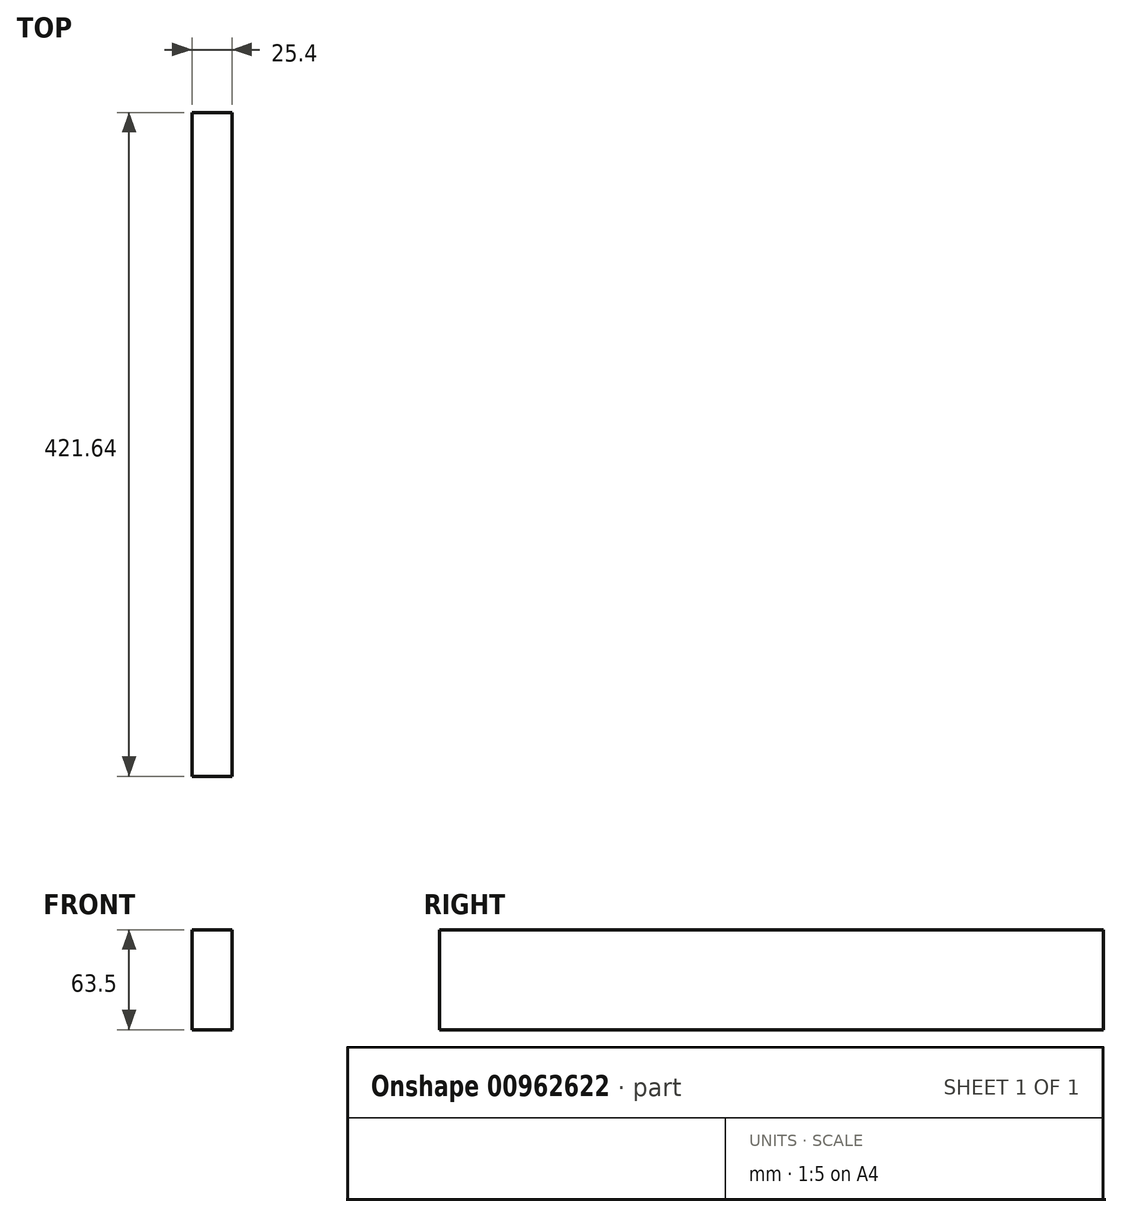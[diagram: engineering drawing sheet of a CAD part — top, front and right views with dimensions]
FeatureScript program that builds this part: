
annotation { "Feature Type Name" : "Feature", "Feature Type Description" : "" }
export const myFeature = defineFeature(function(context is Context, id is Id, definition is map)
    precondition{}
    {
        {
            var Q0;
            Q0=qCreatedBy(makeId("Front.planeOp"),FACE);
            var sketch = newSketch(context, id + "F0", { "sketchPlane" : qUnion([Q0])});
            skLineSegment(sketch, "E0.bottom", {"start": v(12.7, -31.75) * mm, "end": v(-12.7, -31.75) * mm});
            skLineSegment(sketch, "E0.top", {"start": v(12.7, 31.75) * mm, "end": v(-12.7, 31.75) * mm});
            skLineSegment(sketch, "E0.left", {"start": v(12.7, -31.75) * mm, "end": v(12.7, 31.75) * mm});
            skLineSegment(sketch, "E0.right", {"start": v(-12.7, -31.75) * mm, "end": v(-12.7, 31.75) * mm});
            skPoint(sketch, "E0.middle", {"position": v(0, 0) * mm});
            skSolve(sketch);
        }
        {
            var Q0;
            Q0=makeQuery(id+"F0.imprint","IMPRINT",FACE,{"disambiguationData":[TD([[makeQuery(id+"F0.imprint","IMPRINT",EDGE,{"derivedFrom":sQuery(id+"F0.wireOp",EDGE,"E0.bottom")}),-1.0]])]});
            extrude(context, id + "F1", {"entities" : qUnion([Q0]), "depth" : 421.64 * mm, "offsetDistance" : 25.4 * mm});
        }
    });
